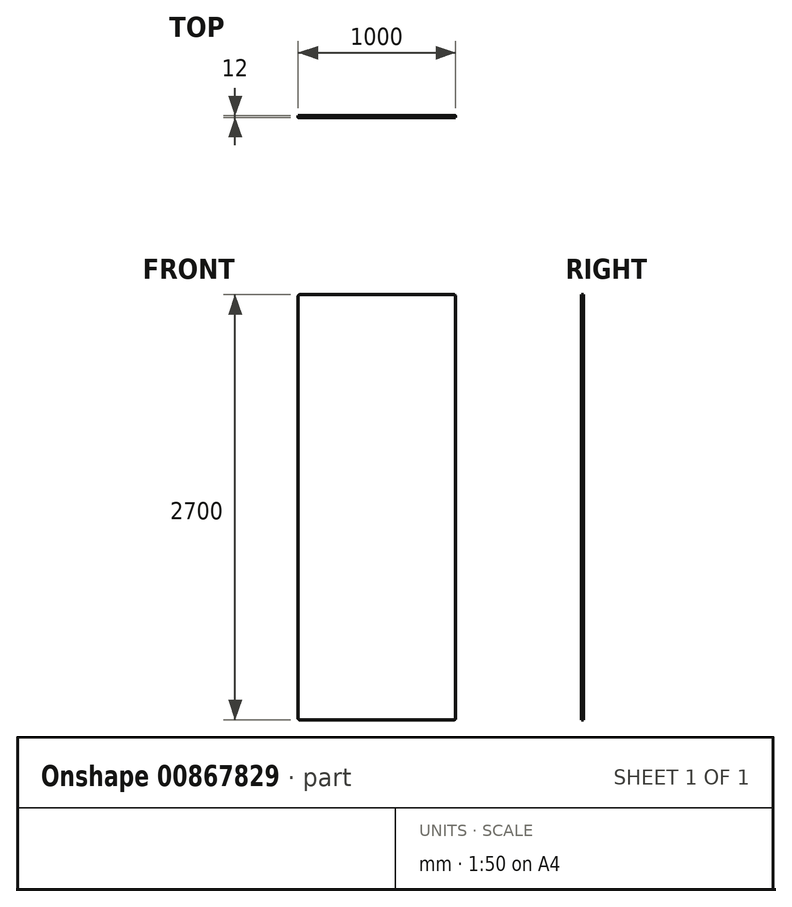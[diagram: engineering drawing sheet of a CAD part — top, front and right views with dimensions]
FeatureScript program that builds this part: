
annotation { "Feature Type Name" : "Feature", "Feature Type Description" : "" }
export const myFeature = defineFeature(function(context is Context, id is Id, definition is map)
    precondition{}
    {
        {
            var Q0;
            Q0=qCreatedBy(makeId("Front.planeOp"),FACE);
            var sketch = newSketch(context, id + "F0", { "sketchPlane" : qUnion([Q0])});
            skLineSegment(sketch, "E0.bottom", {"start": v(-490, 1350) * mm, "end": v(490, 1350) * mm});
            skLineSegment(sketch, "E0.top", {"start": v(-490, -1350) * mm, "end": v(490, -1350) * mm});
            skLineSegment(sketch, "E0.left", {"start": v(-500, 1340) * mm, "end": v(-500, -1340) * mm});
            skLineSegment(sketch, "E0.right", {"start": v(500, 1340) * mm, "end": v(500, -1340) * mm});
            skPoint(sketch, "E0.middle", {"position": v(0, 0) * mm});
            skPoint(sketch, "E1.visualSharp", {"position": v(500, -1350) * mm});
            skArc(sketch, "E1.filletArc", {"start": v(490, -1350) * mm, "mid": v(497.07, -1347.07) * mm, "end": v(500, -1340) * mm});
            skPoint(sketch, "E2.visualSharp", {"position": v(-500, -1350) * mm});
            skArc(sketch, "E2.filletArc", {"start": v(-500, -1340) * mm, "mid": v(-497.07, -1347.07) * mm, "end": v(-490, -1350) * mm});
            skPoint(sketch, "E3.visualSharp", {"position": v(500, 1350) * mm});
            skArc(sketch, "E3.filletArc", {"start": v(500, 1340) * mm, "mid": v(497.07, 1347.07) * mm, "end": v(490, 1350) * mm});
            skPoint(sketch, "E4.visualSharp", {"position": v(-500, 1350) * mm});
            skArc(sketch, "E4.filletArc", {"start": v(-490, 1350) * mm, "mid": v(-497.07, 1347.07) * mm, "end": v(-500, 1340) * mm});
            skSolve(sketch);
        }
        {
            var Q0;
            Q0 = qSketchRegion(id + "F0", true);
            extrude(context, id + "F1", {"entities" : qUnion([Q0]), "depth" : 12 * mm, "offsetDistance" : 25 * mm});
        }
    });
